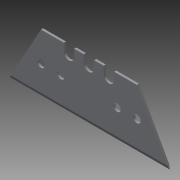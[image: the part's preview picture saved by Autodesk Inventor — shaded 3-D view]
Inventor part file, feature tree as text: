
AUTODESK INVENTOR PART (.ipt)
format: ipt  version: 2014 SP2 (Build 180246200, 246)  size: 140,288 bytes
history: native  units: mm
features: chamfer x2, extrude x1, sketch x1
ambient origin geometry x8: Origin, YZ Plane, XZ Plane, XY Plane, X Axis, Y Axis, Z Axis, Center Point
bodies: Solid1 (feature_tree)
feature tree (4):
  extrude  "Extrusion1"  Depth=1.7mm
  chamfer  "Chamfer1"  Distance=31.5mm
  chamfer  "Chamfer2"  Distance=19.0mm
  sketch  "Sketch1"  dims[d0=52.5mm d1=19.0mm d2=31.5mm d3=19.0mm d4=10.5mm d5=10.5mm d6=7.5mm d7=7.5mm d8=0.0mm d9=7.5mm d10=7.5mm d11=3.4mm d12=3.4mm d13=2.5mm d14=1.7mm d15=1.7mm d16=7.5mm d17=3.4mm d18=1.7mm d19=3.15mm d21=3.15mm d22=2.5mm d23=2.5mm d24=6.5mm d25=9.65mm d26=9.35mm d27=0.0mm d28=5.332895mm d29=2.5mm d30=2.5mm d31=6.5mm d32=0.0mm d33=9.65mm d34=0.7mm d35=0.0mm d38=1.7mm d39=1.7mm d40=1.7mm d41=0.35mm d42=1.0mm d43=60.0deg d44=1.0mm d45=0.35mm d46=60.0deg]
